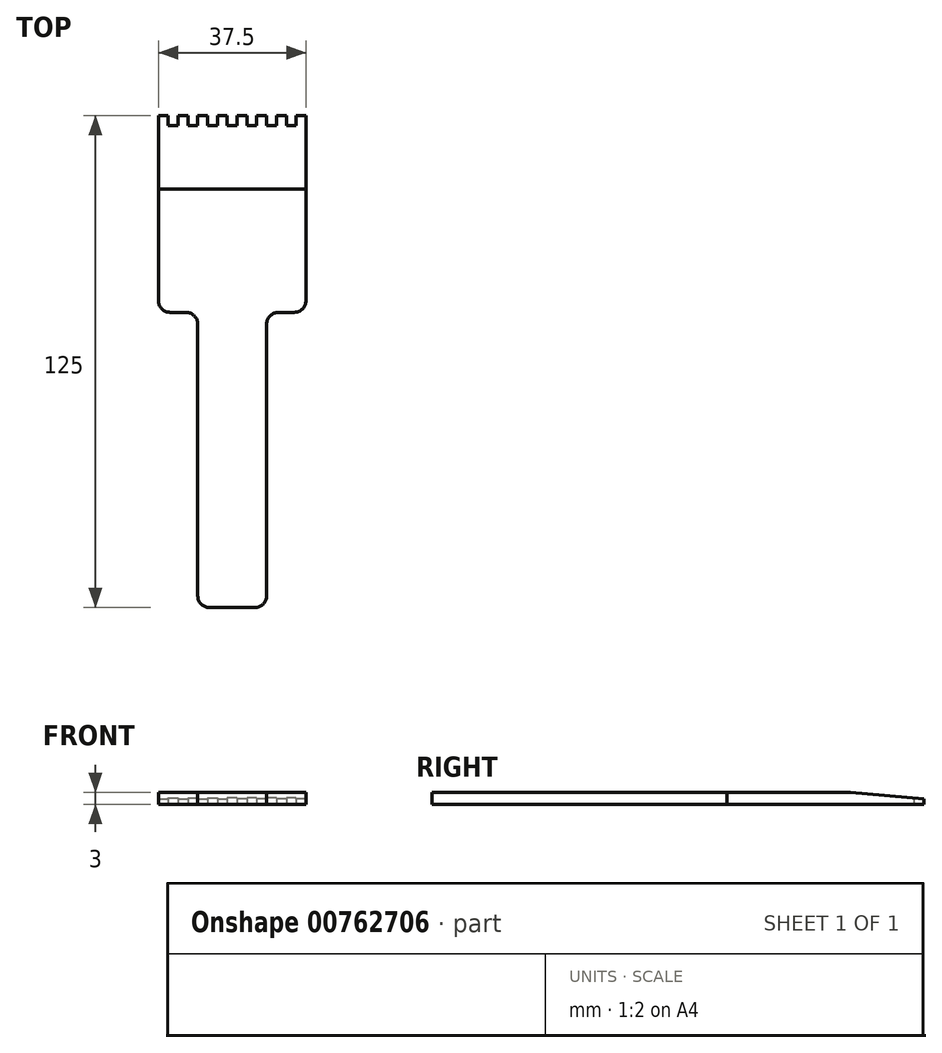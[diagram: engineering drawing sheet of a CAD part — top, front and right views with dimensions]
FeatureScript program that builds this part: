
annotation { "Feature Type Name" : "Feature", "Feature Type Description" : "" }
export const myFeature = defineFeature(function(context is Context, id is Id, definition is map)
    precondition{}
    {
        {
            var Q0;
            Q0=qCreatedBy(makeId("Top.planeOp"),FACE);
            var sketch = newSketch(context, id + "F0", { "sketchPlane" : qUnion([Q0])});
            skPoint(sketch, "E0.middle", {"position": v(0, 0) * mm});
            skLineSegment(sketch, "E1.left", {"start": v(-20, 75) * mm, "end": v(-20, 28) * mm});
            skPoint(sketch, "E1.middle", {"position": v(0, 50) * mm});
            skLineSegment(sketch, "E2", {"start": v(-10, -47) * mm, "end": v(-10, 22) * mm});
            skLineSegment(sketch, "E3", {"start": v(-17, 25) * mm, "end": v(-13, 25) * mm});
            skPoint(sketch, "E4.visualSharp", {"position": v(-10, -50) * mm});
            skArc(sketch, "E4.filletArc", {"start": v(-10, -47) * mm, "mid": v(-9.12, -49.12) * mm, "end": v(-7, -50) * mm});
            skPoint(sketch, "E5.visualSharp", {"position": v(10, -50) * mm});
            skPoint(sketch, "E6.visualSharp", {"position": v(18, 25) * mm});
            skPoint(sketch, "E7.visualSharp", {"position": v(-20, 25) * mm});
            skArc(sketch, "E7.filletArc", {"start": v(-20, 28) * mm, "mid": v(-19.12, 25.88) * mm, "end": v(-17, 25) * mm});
            skPoint(sketch, "E8.visualSharp", {"position": v(10, 25) * mm});
            skPoint(sketch, "E9.visualSharp", {"position": v(-10, 25) * mm});
            skArc(sketch, "E9.filletArc", {"start": v(-10, 22) * mm, "mid": v(-10.88, 24.12) * mm, "end": v(-13, 25) * mm});
            skLineSegment(sketch, "E10.bottom", {"start": v(-20, 75) * mm, "end": v(-17.5, 75) * mm});
            skLineSegment(sketch, "E10.left", {"start": v(-20, 75) * mm, "end": v(-20, 72.5) * mm});
            skLineSegment(sketch, "E10.right", {"start": v(-17.5, 75) * mm, "end": v(-17.5, 72.5) * mm});
            skLineSegment(sketch, "E11.top", {"start": v(-17.5, 72.5) * mm, "end": v(-15, 72.5) * mm});
            skLineSegment(sketch, "E11.right", {"start": v(-15, 75) * mm, "end": v(-15, 72.5) * mm});
            skLineSegment(sketch, "E12.top", {"start": v(-15, 75) * mm, "end": v(-12.5, 75) * mm});
            skLineSegment(sketch, "E12.left", {"start": v(-15, 72.5) * mm, "end": v(-15, 75) * mm});
            skLineSegment(sketch, "E12.right", {"start": v(-12.5, 72.5) * mm, "end": v(-12.5, 75) * mm});
            skLineSegment(sketch, "E13.bottom", {"start": v(-12.5, 72.5) * mm, "end": v(-10, 72.5) * mm});
            skLineSegment(sketch, "E13.right", {"start": v(-10, 72.5) * mm, "end": v(-10, 75) * mm});
            skLineSegment(sketch, "E14.top", {"start": v(-10, 75) * mm, "end": v(-7.5, 75) * mm});
            skLineSegment(sketch, "E14.right", {"start": v(-7.5, 72.5) * mm, "end": v(-7.5, 75) * mm});
            skLineSegment(sketch, "E15.bottom", {"start": v(-7.5, 72.5) * mm, "end": v(-5, 72.5) * mm});
            skLineSegment(sketch, "E15.right", {"start": v(-5, 72.5) * mm, "end": v(-5, 75) * mm});
            skLineSegment(sketch, "E16.top", {"start": v(-5, 75) * mm, "end": v(-2.5, 75) * mm});
            skLineSegment(sketch, "E16.right", {"start": v(-2.5, 72.5) * mm, "end": v(-2.5, 75) * mm});
            skLineSegment(sketch, "E17.bottom", {"start": v(-2.5, 72.5) * mm, "end": v(-1.25, 72.5) * mm});
            skLineSegment(sketch, "E18", {"start": v(-7, -50) * mm, "end": v(-1.25, -50) * mm});
            skLineSegment(sketch, "E19.MirrorCS", {"start": v(4.5, -50) * mm, "end": v(-1.25, -50) * mm});
            skArc(sketch, "E20.MirrorCS", {"start": v(7.5, -47) * mm, "mid": v(6.62, -49.12) * mm, "end": v(4.5, -50) * mm});
            skLineSegment(sketch, "E21.MirrorCS", {"start": v(7.5, -47) * mm, "end": v(7.5, 22) * mm});
            skArc(sketch, "E22.MirrorCS", {"start": v(7.5, 22) * mm, "mid": v(8.38, 24.12) * mm, "end": v(10.5, 25) * mm});
            skLineSegment(sketch, "E23.MirrorCS", {"start": v(14.5, 25) * mm, "end": v(10.5, 25) * mm});
            skArc(sketch, "E24.MirrorCS", {"start": v(17.5, 28) * mm, "mid": v(16.62, 25.88) * mm, "end": v(14.5, 25) * mm});
            skLineSegment(sketch, "E25.MirrorCS", {"start": v(17.5, 75) * mm, "end": v(17.5, 28) * mm});
            skLineSegment(sketch, "E26.MirrorCS", {"start": v(0, 72.5) * mm, "end": v(-1.25, 72.5) * mm});
            skLineSegment(sketch, "E27.MirrorCS", {"start": v(0, 72.5) * mm, "end": v(0, 75) * mm});
            skLineSegment(sketch, "E28.MirrorCS", {"start": v(2.5, 75) * mm, "end": v(0, 75) * mm});
            skLineSegment(sketch, "E29.MirrorCS", {"start": v(2.5, 72.5) * mm, "end": v(2.5, 75) * mm});
            skLineSegment(sketch, "E30.MirrorCS", {"start": v(5, 72.5) * mm, "end": v(2.5, 72.5) * mm});
            skLineSegment(sketch, "E31.MirrorCS", {"start": v(5, 72.5) * mm, "end": v(5, 75) * mm});
            skLineSegment(sketch, "E32.MirrorCS", {"start": v(7.5, 75) * mm, "end": v(5, 75) * mm});
            skLineSegment(sketch, "E33.MirrorCS", {"start": v(7.5, 72.5) * mm, "end": v(7.5, 75) * mm});
            skLineSegment(sketch, "E34.MirrorCS", {"start": v(10, 72.5) * mm, "end": v(7.5, 72.5) * mm});
            skLineSegment(sketch, "E35.MirrorCS", {"start": v(10, 72.5) * mm, "end": v(10, 75) * mm});
            skLineSegment(sketch, "E36.MirrorCS", {"start": v(12.5, 75) * mm, "end": v(10, 75) * mm});
            skLineSegment(sketch, "E37.MirrorCS", {"start": v(12.5, 75) * mm, "end": v(12.5, 72.5) * mm});
            skLineSegment(sketch, "E38.MirrorCS", {"start": v(15, 72.5) * mm, "end": v(12.5, 72.5) * mm});
            skLineSegment(sketch, "E39.MirrorCS", {"start": v(15, 75) * mm, "end": v(15, 72.5) * mm});
            skLineSegment(sketch, "E40.MirrorCS", {"start": v(17.5, 75) * mm, "end": v(15, 75) * mm});
            skSolve(sketch);
        }
        {
            var Q0;
            Q0=makeQuery(id+"F0.imprint","IMPRINT",FACE,{"disambiguationData":[TD([[makeQuery(id+"F0.imprint","IMPRINT",EDGE,{"derivedFrom":sQuery(id+"F0.wireOp",EDGE,"E1.left")}),1.0]])]});
            extrude(context, id + "F1", {"entities" : qUnion([Q0]), "depth" : 3 * mm, "offsetDistance" : 25 * mm});
        }
        {
            var Q0;
            Q0=makeQuery(id+"F1.opExtrude","SWEPT_FACE",FACE,{"disambiguationData":[OSD([sQuery(id+"F0.wireOp",EDGE,"E25.MirrorCS")])]});
            var sketch = newSketch(context, id + "F2", { "sketchPlane" : qUnion([Q0])});
            skLineSegment(sketch, "E41", {"start": v(78.92, 1.07) * mm, "end": v(41.32, 4.28) * mm});
            skLineSegment(sketch, "E42", {"start": v(41.32, 4.28) * mm, "end": v(79.07, 6.6) * mm});
            skLineSegment(sketch, "E43", {"start": v(79.07, 6.6) * mm, "end": v(78.92, 1.07) * mm});
            skSolve(sketch);
        }
        {
            var Q0;
            {var subQ1=sQuery(id+"F2.wireOp",EDGE,"E42");Q0=makeQuery(id+"F2.imprint","IMPRINT",FACE,{"disambiguationData":[TD([[makeQuery(id+"F2.imprint","IMPRINT",EDGE,{"derivedFrom":subQ1}),-1.0]])]});}
            var Q1;
            {var subQ0=sQuery(id+"F2.wireOp",EDGE,"E41");var subQ1=sQuery(id+"F0.wireOp",EDGE,"E25.MirrorCS");var subQ4=makeQuery(id+"F1.opExtrude","CAP_EDGE",EDGE,{"disambiguationData":[OSD([subQ1])],"isStart":false});var subQ5=makeQuery(id+"F2.imprint","INTERSECT",VERTEX,{"derivedFrom":[subQ4,subQ0]});Q1=makeQuery(id+"F2.imprint","IMPRINT",FACE,{"disambiguationData":[TD([[makeQuery(id+"F2.imprint","IMPRINT",EDGE,{"disambiguationData":[TD([[subQ5,1.0]])],"derivedFrom":subQ0}),-1.0]])]});}
            extrude(context, id + "F3", {"entities" : qUnion([Q0, Q1]), "operationType" : NewBodyOperationType.REMOVE, "oppositeDirection" : true, "depth" : 65 * mm, "offsetDistance" : 25 * mm});
        }
    });
